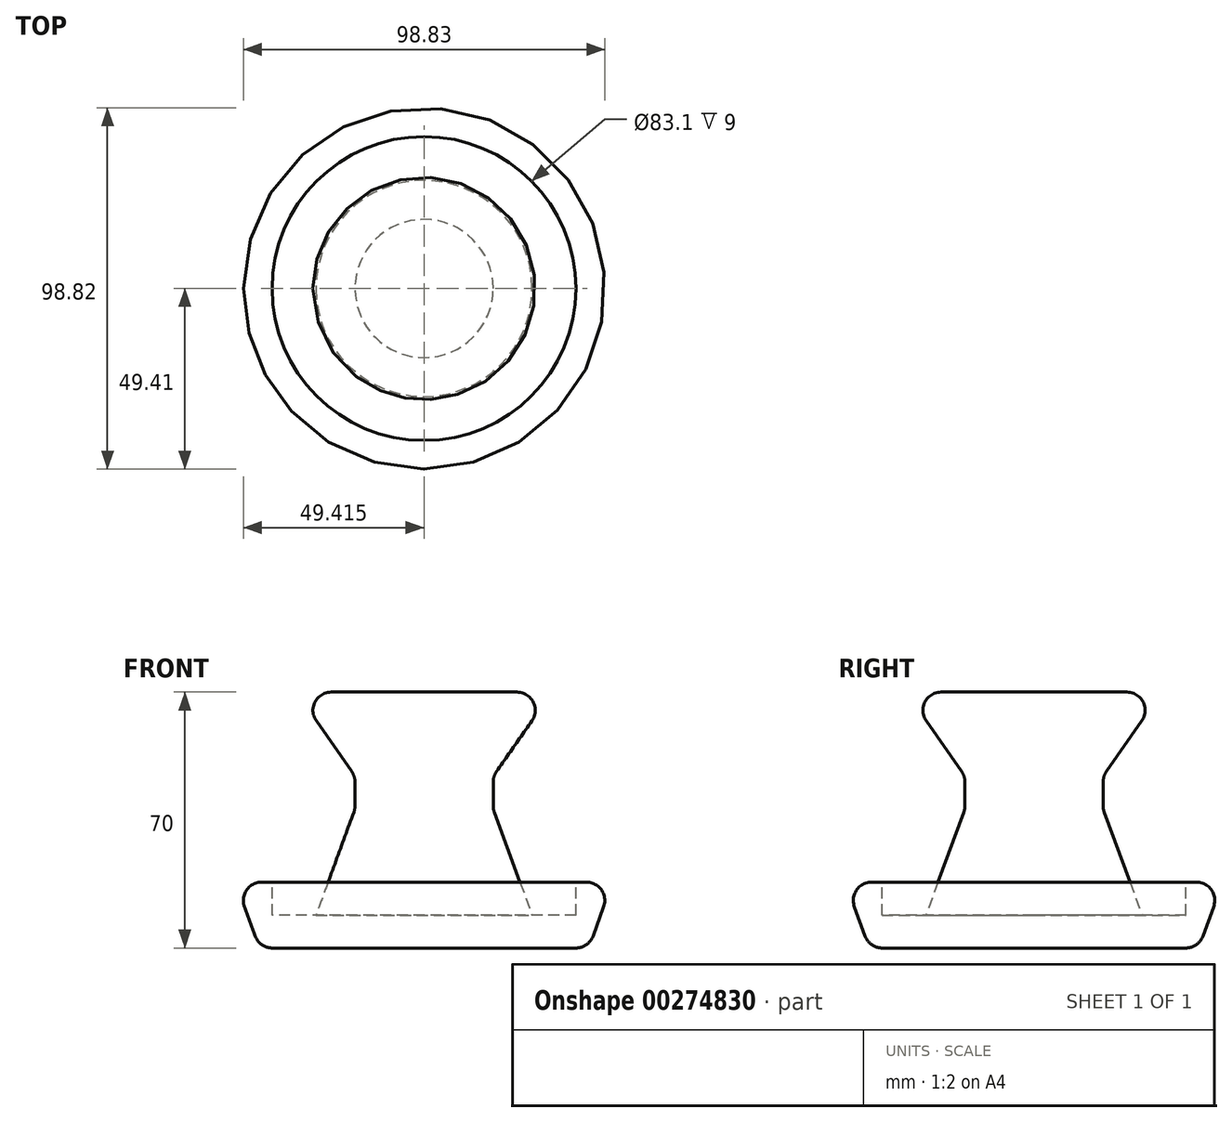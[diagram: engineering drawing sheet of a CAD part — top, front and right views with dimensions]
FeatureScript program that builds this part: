
annotation { "Feature Type Name" : "Feature", "Feature Type Description" : "" }
export const myFeature = defineFeature(function(context is Context, id is Id, definition is map)
    precondition{}
    {
        {
            var Q0;
            Q0=qCreatedBy(makeId("Front.planeOp"),FACE);
            var sketch = newSketch(context, id + "F0", { "sketchPlane" : qUnion([Q0])});
            skLineSegment(sketch, "E0", {"start": v(31.4, -38) * mm, "end": v(-13.6, -38) * mm});
            skLineSegment(sketch, "E1", {"start": v(-13.6, -38) * mm, "end": v(-20.15, -20) * mm});
            skLineSegment(sketch, "E2", {"start": v(-20.15, -20) * mm, "end": v(-10.15, -20) * mm});
            skLineSegment(sketch, "E3", {"start": v(-10.15, -20) * mm, "end": v(-10.15, -29) * mm});
            skLineSegment(sketch, "E4", {"start": v(-10.15, -29) * mm, "end": v(1.85, -29) * mm});
            skLineSegment(sketch, "E5", {"start": v(1.85, -29) * mm, "end": v(12.5, 0) * mm});
            skLineSegment(sketch, "E6", {"start": v(12.5, 0) * mm, "end": v(12.5, 9) * mm});
            skLineSegment(sketch, "E7", {"start": v(12.5, 9) * mm, "end": v(-3.6, 32) * mm});
            skLineSegment(sketch, "E8", {"start": v(-3.6, 32) * mm, "end": v(31.4, 32) * mm});
            skLineSegment(sketch, "E9", {"start": v(31.4, 32) * mm, "end": v(31.4, -38) * mm});
            skSolve(sketch);
        }
        {
            var Q0;
            Q0=makeQuery(id+"F0.imprint","IMPRINT",FACE,{"disambiguationData":[TD([[makeQuery(id+"F0.imprint","IMPRINT",EDGE,{"derivedFrom":sQuery(id+"F0.wireOp",EDGE,"E0")}),-1.0]])]});
            var Q1;
            Q1=sQuery(id+"F0.wireOp",EDGE,"E9");
            revolve(context, id + "F1", {"entities" : qUnion([Q0]), "axis" : qUnion([Q1]), "revolveType" : RevolveType.ONE_DIRECTION, "angle" : 360 * degree});
        }
        {
            var Q0;
            Q0=makeQuery(id+"F1.opRevolve","SWEPT_EDGE",EDGE,{"disambiguationData":[OSD([sQuery(id+"F0.wireOp",EDGE,"E7"),sQuery(id+"F0.wireOp",EDGE,"E8")])]});
            var Q1;
            Q1=makeQuery(id+"F1.opRevolve","SWEPT_EDGE",EDGE,{"disambiguationData":[OSD([sQuery(id+"F0.wireOp",EDGE,"E1"),sQuery(id+"F0.wireOp",EDGE,"E2")])]});
            fillet(context, id + "F2", {"entities" : qUnion([Q0, Q1]), "radius" : 5 * mm, "tangentPropagation" : true, "allowEdgeOverflow" : false});
        }
        {
            var Q0;
            Q0=makeQuery(id+"F1.opRevolve","SWEPT_EDGE",EDGE,{"disambiguationData":[OSD([sQuery(id+"F0.wireOp",EDGE,"E5"),sQuery(id+"F0.wireOp",EDGE,"E6")])]});
            var Q1;
            Q1=makeQuery(id+"F1.opRevolve","SWEPT_EDGE",EDGE,{"disambiguationData":[OSD([sQuery(id+"F0.wireOp",EDGE,"E6"),sQuery(id+"F0.wireOp",EDGE,"E7")])]});
            fillet(context, id + "F3", {"entities" : qUnion([Q0, Q1]), "radius" : 5 * mm, "tangentPropagation" : true, "allowEdgeOverflow" : false});
        }
        {
            var Q0;
            Q0=makeQuery(id+"F1.opRevolve","SWEPT_EDGE",EDGE,{"disambiguationData":[OSD([sQuery(id+"F0.wireOp",EDGE,"E0"),sQuery(id+"F0.wireOp",EDGE,"E1")])]});
            fillet(context, id + "F4", {"entities" : qUnion([Q0]), "radius" : 5 * mm, "tangentPropagation" : true, "allowEdgeOverflow" : false});
        }
    });
